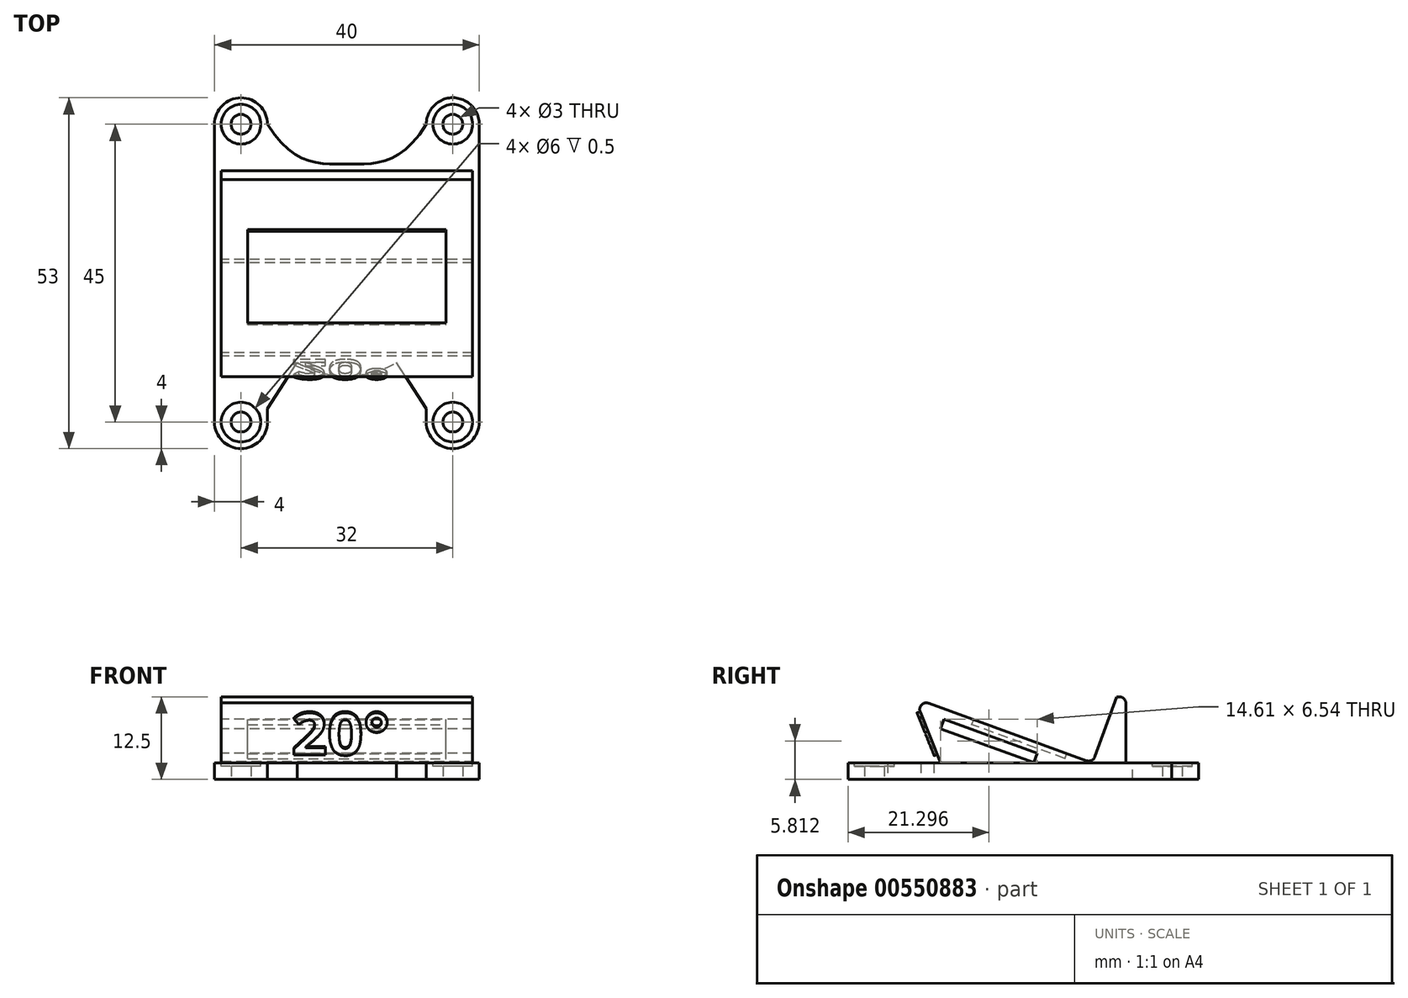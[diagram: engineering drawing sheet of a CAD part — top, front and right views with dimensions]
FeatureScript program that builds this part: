
annotation { "Feature Type Name" : "Feature", "Feature Type Description" : "" }
export const myFeature = defineFeature(function(context is Context, id is Id, definition is map)
    precondition{}
    {
        {
            var Q0;
            Q0=qCreatedBy(makeId("Top.planeOp"),FACE);
            var sketch = newSketch(context, id + "F0", { "sketchPlane" : qUnion([Q0])});
            skCircle(sketch, "E0", {"center": v(-16, 22.5) * mm, "radius": 4 * mm});
            skCircle(sketch, "E1", {"center": v(16, 22.5) * mm, "radius": 4 * mm});
            skCircle(sketch, "E2", {"center": v(-16, -22.5) * mm, "radius": 4 * mm});
            skCircle(sketch, "E3", {"center": v(16, -22.5) * mm, "radius": 4 * mm});
            skLineSegment(sketch, "E4", {"start": v(-20, 22.5) * mm, "end": v(-20, -22.5) * mm});
            skLineSegment(sketch, "E5", {"start": v(20, 22.55) * mm, "end": v(20, -22.5) * mm});
            skLineSegment(sketch, "E6", {"start": v(-12, -22.5) * mm, "end": v(-12, -20.5) * mm});
            skLineSegment(sketch, "E7", {"start": v(12, -22.5) * mm, "end": v(12, -20.5) * mm});
            skLineSegment(sketch, "E8", {"start": v(-12, -20.5) * mm, "end": v(-7.5, -13.5) * mm});
            skLineSegment(sketch, "E9", {"start": v(12, -20.5) * mm, "end": v(7.5, -13.5) * mm});
            skFitSpline(sketch, "E10", {"points": [v(-7.5, -13.5) * mm, v(0, -15.5) * mm, v(7.5, -13.5) * mm], "startDerivative": vector(15, -9) * mm, "endDerivative": vector(15, 9) * mm});
            skFitSpline(sketch, "E11", {"points": [v(-12, 22.5) * mm, v(0, 16.5) * mm, v(12, 22.5) * mm], "startDerivative": vector(24, -39) * mm, "endDerivative": vector(24, 39) * mm});
            skSolve(sketch);
        }
        {
            var Q0;
            Q0 = qSketchRegion(id + "F0", true);
            extrude(context, id + "F1", {"entities" : qUnion([Q0]), "depth" : 2.5 * mm, "offsetDistance" : 25 * mm});
        }
        {
            var Q0;
            Q0=qCreatedBy(makeId("Right.planeOp"),FACE);
            var sketch = newSketch(context, id + "F2", { "sketchPlane" : qUnion([Q0])});
            skLineSegment(sketch, "E12", {"start": v(15.5, 10.16) * mm, "end": v(15.5, 2.5) * mm});
            skLineSegment(sketch, "E13", {"start": v(15.5, 2.5) * mm, "end": v(-12.5, 2.5) * mm});
            skLineSegment(sketch, "E14", {"start": v(-12.5, 2.5) * mm, "end": v(-16.5, 12.5) * mm});
            skLineSegment(sketch, "E15", {"start": v(-16.5, 12.5) * mm, "end": v(15.5, 12.5) * mm});
            skLineSegment(sketch, "E16", {"start": v(15.5, 12.5) * mm, "end": v(15.5, 10.16) * mm});
            skSolve(sketch);
        }
        {
            var Q0;
            Q0 = qSketchRegion(id + "F2", true);
            extrude(context, id + "F3", {"entities" : qUnion([Q0]), "endBound" : BoundingType.SYMMETRIC, "depth" : 38 * mm, "offsetDistance" : 25 * mm});
        }
        {
            var Q0;
            Q0=makeQuery(id+"F3.opExtrude","CAP_FACE",FACE,{"disambiguationData":[OSD([sQuery(id+"F2.wireOp",EDGE,"E12"),sQuery(id+"F2.wireOp",EDGE,"E13"),sQuery(id+"F2.wireOp",EDGE,"E14"),sQuery(id+"F2.wireOp",EDGE,"E15"),sQuery(id+"F2.wireOp",EDGE,"E16")])],"isStart":true});
            var sketch = newSketch(context, id + "F4", { "sketchPlane" : qUnion([Q0])});
            skLineSegment(sketch, "E17", {"start": v(-14.11, 12.5) * mm, "end": v(-10.47, 2.5) * mm});
            skLineSegment(sketch, "E18", {"start": v(-10.47, 2.5) * mm, "end": v(17, 12.5) * mm});
            skLineSegment(sketch, "E19", {"start": v(17, 12.5) * mm, "end": v(-14.11, 12.5) * mm});
            skSolve(sketch);
        }
        {
            var Q0;
            Q0 = qSketchRegion(id + "F4", true);
            extrude(context, id + "F5", {"entities" : qUnion([Q0]), "oppositeDirection" : true, "depth" : 40 * mm, "offsetDistance" : 25 * mm});
        }
        {
            var Q0;
            Q0=makeQuery(id+"F5.opExtrude","SWEPT_BODY",BODY,{"disambiguationData":[OSD([sQuery(id+"F4.wireOp",EDGE,"E17"),sQuery(id+"F4.wireOp",EDGE,"E18"),sQuery(id+"F4.wireOp",EDGE,"E19")])]});
            var Q1;
            Q1=makeQuery(id+"F3.opExtrude","SWEPT_BODY",BODY,{"disambiguationData":[OSD([sQuery(id+"F2.wireOp",EDGE,"E12"),sQuery(id+"F2.wireOp",EDGE,"E13"),sQuery(id+"F2.wireOp",EDGE,"E14"),sQuery(id+"F2.wireOp",EDGE,"E15"),sQuery(id+"F2.wireOp",EDGE,"E16")])]});
            booleanBodies(context, id + "F6", {"operationType" : BooleanOperationType.SUBTRACTION, "tools" : qUnion([Q0]), "targets" : qUnion([Q1])});
        }
        {
            var Q0;
            Q0=sQuery(id+"F0.wireOp",VERTEX,"E0.center");
            var Q1;
            Q1=sQuery(id+"F0.wireOp",VERTEX,"E1.center");
            var Q2;
            Q2=sQuery(id+"F0.wireOp",VERTEX,"E2.center");
            var Q3;
            Q3=sQuery(id+"F0.wireOp",VERTEX,"E3.center");
            var Q4;
            Q4=makeQuery(id+"F1.opExtrude","SWEPT_BODY",BODY,{"disambiguationData":[OSD([sQuery(id+"F0.wireOp",EDGE,"E0"),sQuery(id+"F0.wireOp",EDGE,"E1"),sQuery(id+"F0.wireOp",EDGE,"E2"),sQuery(id+"F0.wireOp",EDGE,"E3"),sQuery(id+"F0.wireOp",EDGE,"E4"),sQuery(id+"F0.wireOp",EDGE,"E5"),sQuery(id+"F0.wireOp",EDGE,"E6"),sQuery(id+"F0.wireOp",EDGE,"E7"),sQuery(id+"F0.wireOp",EDGE,"E8"),sQuery(id+"F0.wireOp",EDGE,"E9"),sQuery(id+"F0.wireOp",EDGE,"E10"),sQuery(id+"F0.wireOp",EDGE,"E11")])]});
            hole(context, id + "F7", {"style" : HoleStyle.SIMPLE, "endStyle" : HoleEndStyle.THROUGH, "oppositeDirection" : true, "holeDiameter" : 3 * mm, "tappedDepth" : 12 * mm, "tapClearance" : 3, "locations" : qUnion([Q0, Q1, Q2, Q3]), "scope" : qUnion([Q4])});
        }
        {
            var Q0;
            Q0=makeQuery(id+"F1.opExtrude","CAP_FACE",FACE,{"disambiguationData":[OSD([sQuery(id+"F0.wireOp",EDGE,"E0"),sQuery(id+"F0.wireOp",EDGE,"E1"),sQuery(id+"F0.wireOp",EDGE,"E2"),sQuery(id+"F0.wireOp",EDGE,"E3"),sQuery(id+"F0.wireOp",EDGE,"E4"),sQuery(id+"F0.wireOp",EDGE,"E5"),sQuery(id+"F0.wireOp",EDGE,"E6"),sQuery(id+"F0.wireOp",EDGE,"E7"),sQuery(id+"F0.wireOp",EDGE,"E8"),sQuery(id+"F0.wireOp",EDGE,"E9"),sQuery(id+"F0.wireOp",EDGE,"E10"),sQuery(id+"F0.wireOp",EDGE,"E11")])],"isStart":false});
            var sketch = newSketch(context, id + "F8", { "sketchPlane" : qUnion([Q0])});
            skCircle(sketch, "E20", {"center": v(-16, 22.5) * mm, "radius": 3 * mm});
            skCircle(sketch, "E21", {"center": v(16, 22.5) * mm, "radius": 3 * mm});
            skCircle(sketch, "E22", {"center": v(-16, -22.5) * mm, "radius": 3 * mm});
            skCircle(sketch, "E23", {"center": v(16, -22.5) * mm, "radius": 3 * mm});
            skSolve(sketch);
        }
        {
            var Q0;
            Q0 = qSketchRegion(id + "F8", true);
            extrude(context, id + "F9", {"entities" : qUnion([Q0]), "oppositeDirection" : true, "depth" : 0.5 * mm, "offsetDistance" : 25 * mm});
        }
        {
            var Q0;
            Q0=makeQuery(id+"F9.opExtrude","SWEPT_BODY",BODY,{"disambiguationData":[OSD([sQuery(id+"F8.wireOp",EDGE,"E20")])]});
            var Q1;
            Q1=makeQuery(id+"F9.opExtrude","SWEPT_BODY",BODY,{"disambiguationData":[OSD([sQuery(id+"F8.wireOp",EDGE,"E21")])]});
            var Q2;
            Q2=makeQuery(id+"F9.opExtrude","SWEPT_BODY",BODY,{"disambiguationData":[OSD([sQuery(id+"F8.wireOp",EDGE,"E22")])]});
            var Q3;
            Q3=makeQuery(id+"F9.opExtrude","SWEPT_BODY",BODY,{"disambiguationData":[OSD([sQuery(id+"F8.wireOp",EDGE,"E23")])]});
            var Q4;
            Q4=makeQuery(id+"F1.opExtrude","SWEPT_BODY",BODY,{"disambiguationData":[OSD([sQuery(id+"F0.wireOp",EDGE,"E0"),sQuery(id+"F0.wireOp",EDGE,"E1"),sQuery(id+"F0.wireOp",EDGE,"E2"),sQuery(id+"F0.wireOp",EDGE,"E3"),sQuery(id+"F0.wireOp",EDGE,"E4"),sQuery(id+"F0.wireOp",EDGE,"E5"),sQuery(id+"F0.wireOp",EDGE,"E6"),sQuery(id+"F0.wireOp",EDGE,"E7"),sQuery(id+"F0.wireOp",EDGE,"E8"),sQuery(id+"F0.wireOp",EDGE,"E9"),sQuery(id+"F0.wireOp",EDGE,"E10"),sQuery(id+"F0.wireOp",EDGE,"E11")])]});
            booleanBodies(context, id + "F10", {"operationType" : BooleanOperationType.SUBTRACTION, "tools" : qUnion([Q0, Q1, Q2, Q3]), "targets" : qUnion([Q4])});
        }
        {
            var Q0;
            Q0=makeQuery(id+"F6.opBoolean","COPY",FACE,{"derivedFrom":makeQuery(id+"F5.opExtrude","SWEPT_FACE",FACE,{"disambiguationData":[OSD([sQuery(id+"F4.wireOp",EDGE,"E18")])]})});
            var sketch = newSketch(context, id + "F11", { "sketchPlane" : qUnion([Q0])});
            skLineSegment(sketch, "E24.bottom", {"start": v(-15, 4.84) * mm, "end": v(15, 4.84) * mm});
            skLineSegment(sketch, "E24.top", {"start": v(-15, -10.16) * mm, "end": v(15, -10.16) * mm});
            skLineSegment(sketch, "E24.left", {"start": v(-15, 4.84) * mm, "end": v(-15, -10.16) * mm});
            skLineSegment(sketch, "E24.right", {"start": v(15, 4.84) * mm, "end": v(15, -10.16) * mm});
            skSolve(sketch);
        }
        {
            var Q0;
            Q0 = qSketchRegion(id + "F11", true);
            extrude(context, id + "F12", {"entities" : qUnion([Q0]), "oppositeDirection" : true, "depth" : 0.8 * mm, "offsetDistance" : 25 * mm});
        }
        {
            var Q0;
            Q0=makeQuery(id+"F12.opExtrude","SWEPT_BODY",BODY,{"disambiguationData":[OSD([sQuery(id+"F11.wireOp",EDGE,"E24.bottom"),sQuery(id+"F11.wireOp",EDGE,"E24.top"),sQuery(id+"F11.wireOp",EDGE,"E24.left"),sQuery(id+"F11.wireOp",EDGE,"E24.right")])]});
            var Q1;
            Q1=makeQuery(id+"F6.opBoolean","SPLIT",BODY,{"disambiguationData":[OD(1.0)],"derivedFrom":makeQuery(id+"F3.opExtrude","SWEPT_BODY",BODY,{"disambiguationData":[OSD([sQuery(id+"F2.wireOp",EDGE,"E12"),sQuery(id+"F2.wireOp",EDGE,"E13"),sQuery(id+"F2.wireOp",EDGE,"E14"),sQuery(id+"F2.wireOp",EDGE,"E15"),sQuery(id+"F2.wireOp",EDGE,"E16")])]})});
            booleanBodies(context, id + "F13", {"operationType" : BooleanOperationType.SUBTRACTION, "tools" : qUnion([Q0]), "targets" : qUnion([Q1])});
        }
        {
            var Q0;
            {var subQ0=sQuery(id+"F2.wireOp",EDGE,"E13");var subQ1=sQuery(id+"F2.wireOp",EDGE,"E14");Q0=makeQuery(id+"F6.opBoolean","SPLIT",FACE,{"disambiguationData":[TD([makeQuery(id+"F3.opExtrude","SWEPT_FACE",FACE,{"disambiguationData":[OSD([subQ1])]})])],"derivedFrom":makeQuery(id+"F3.opExtrude","CAP_FACE",FACE,{"disambiguationData":[OSD([sQuery(id+"F2.wireOp",EDGE,"E12"),subQ0,subQ1,sQuery(id+"F2.wireOp",EDGE,"E15"),sQuery(id+"F2.wireOp",EDGE,"E16")])],"isStart":true})});}
            var sketch = newSketch(context, id + "F14", { "sketchPlane" : qUnion([Q0])});
            skLineSegment(sketch, "E25", {"start": v(-2.1, 3.95) * mm, "end": v(12, 9.08) * mm});
            skLineSegment(sketch, "E26", {"start": v(12, 9.08) * mm, "end": v(12.5, 7.67) * mm});
            skLineSegment(sketch, "E27", {"start": v(12.5, 7.67) * mm, "end": v(-1.59, 2.54) * mm});
            skLineSegment(sketch, "E28", {"start": v(-1.59, 2.54) * mm, "end": v(-2.1, 3.95) * mm});
            skSolve(sketch);
        }
        {
            var Q0;
            Q0 = qSketchRegion(id + "F14", true);
            extrude(context, id + "F15", {"entities" : qUnion([Q0]), "oppositeDirection" : true, "depth" : 40 * mm, "offsetDistance" : 25 * mm});
        }
        {
            var Q0;
            Q0=makeQuery(id+"F15.opExtrude","SWEPT_BODY",BODY,{"disambiguationData":[OSD([sQuery(id+"F14.wireOp",EDGE,"E25"),sQuery(id+"F14.wireOp",EDGE,"E26"),sQuery(id+"F14.wireOp",EDGE,"E27"),sQuery(id+"F14.wireOp",EDGE,"E28")])]});
            var Q1;
            Q1=makeQuery(id+"F6.opBoolean","SPLIT",BODY,{"disambiguationData":[OD(1.0)],"derivedFrom":makeQuery(id+"F3.opExtrude","SWEPT_BODY",BODY,{"disambiguationData":[OSD([sQuery(id+"F2.wireOp",EDGE,"E12"),sQuery(id+"F2.wireOp",EDGE,"E13"),sQuery(id+"F2.wireOp",EDGE,"E14"),sQuery(id+"F2.wireOp",EDGE,"E15"),sQuery(id+"F2.wireOp",EDGE,"E16")])]})});
            booleanBodies(context, id + "F16", {"operationType" : BooleanOperationType.SUBTRACTION, "tools" : qUnion([Q0]), "targets" : qUnion([Q1])});
        }
        {
            var Q0;
            Q0=makeQuery(id+"F1.opExtrude","SWEPT_BODY",BODY,{"disambiguationData":[OSD([sQuery(id+"F0.wireOp",EDGE,"E0"),sQuery(id+"F0.wireOp",EDGE,"E1"),sQuery(id+"F0.wireOp",EDGE,"E2"),sQuery(id+"F0.wireOp",EDGE,"E3"),sQuery(id+"F0.wireOp",EDGE,"E4"),sQuery(id+"F0.wireOp",EDGE,"E5"),sQuery(id+"F0.wireOp",EDGE,"E6"),sQuery(id+"F0.wireOp",EDGE,"E7"),sQuery(id+"F0.wireOp",EDGE,"E8"),sQuery(id+"F0.wireOp",EDGE,"E9"),sQuery(id+"F0.wireOp",EDGE,"E10"),sQuery(id+"F0.wireOp",EDGE,"E11")])]});
            var Q1;
            Q1=makeQuery(id+"F6.opBoolean","SPLIT",BODY,{"disambiguationData":[OD(0.0)],"derivedFrom":makeQuery(id+"F3.opExtrude","SWEPT_BODY",BODY,{"disambiguationData":[OSD([sQuery(id+"F2.wireOp",EDGE,"E12"),sQuery(id+"F2.wireOp",EDGE,"E13"),sQuery(id+"F2.wireOp",EDGE,"E14"),sQuery(id+"F2.wireOp",EDGE,"E15"),sQuery(id+"F2.wireOp",EDGE,"E16")])]})});
            var Q2;
            Q2=makeQuery(id+"F6.opBoolean","SPLIT",BODY,{"disambiguationData":[OD(1.0)],"derivedFrom":makeQuery(id+"F3.opExtrude","SWEPT_BODY",BODY,{"disambiguationData":[OSD([sQuery(id+"F2.wireOp",EDGE,"E12"),sQuery(id+"F2.wireOp",EDGE,"E13"),sQuery(id+"F2.wireOp",EDGE,"E14"),sQuery(id+"F2.wireOp",EDGE,"E15"),sQuery(id+"F2.wireOp",EDGE,"E16")])]})});
            booleanBodies(context, id + "F17", {"operationType" : BooleanOperationType.UNION, "tools" : qUnion([Q0, Q1, Q2])});
        }
        {
            var Q0;
            Q0=makeQuery(id+"F3.opExtrude","SWEPT_EDGE",EDGE,{"disambiguationData":[OSD([sQuery(id+"F2.wireOp",EDGE,"E13"),sQuery(id+"F2.wireOp",EDGE,"E14")])]});
            var Q1;
            Q1=makeQuery(id+"F6.opBoolean","INTERSECT",EDGE,{"derivedFrom":[makeQuery(id+"F3.opExtrude","SWEPT_FACE",FACE,{"disambiguationData":[OSD([sQuery(id+"F2.wireOp",EDGE,"E14")])]}),makeQuery(id+"F5.opExtrude","SWEPT_FACE",FACE,{"disambiguationData":[OSD([sQuery(id+"F4.wireOp",EDGE,"E18")])]})]});
            var Q2;
            Q2=makeQuery(id+"F3.opExtrude","SWEPT_EDGE",EDGE,{"disambiguationData":[OSD([sQuery(id+"F2.wireOp",EDGE,"E15"),sQuery(id+"F2.wireOp",EDGE,"E16")])]});
            var Q3;
            {var subQ0=sQuery(id+"F2.wireOp",EDGE,"E13");var subQ2=sQuery(id+"F4.wireOp",EDGE,"E18");var subQ3=sQuery(id+"F4.wireOp",EDGE,"E17");var subQ4=makeQuery(id+"F5.opExtrude","SWEPT_EDGE",EDGE,{"disambiguationData":[OSD([subQ0,subQ3,subQ2])]});Q3=makeQuery(id+"F17.opBoolean","MERGE",EDGE,{"derivedFrom":[makeQuery(id+"F6.opBoolean","COPY",EDGE,{"disambiguationData":[topologyDisambiguationEdgeConnected([makeQuery(id+"F5.opExtrude","SWEPT_FACE",FACE,{"disambiguationData":[OSD([subQ3])]})])],"derivedFrom":subQ4}),makeQuery(id+"F6.opBoolean","COPY",EDGE,{"disambiguationData":[topologyDisambiguationEdgeConnected([makeQuery(id+"F5.opExtrude","SWEPT_FACE",FACE,{"disambiguationData":[OSD([subQ2])]})])],"derivedFrom":subQ4})]});}
            fillet(context, id + "F18", {"entities" : qUnion([Q0, Q1, Q2, Q3]), "radius" : 1 * mm, "tangentPropagation" : true, "allowEdgeOverflow" : false});
        }
        {
            var Q0;
            Q0=makeQuery(id+"F3.opExtrude","SWEPT_FACE",FACE,{"disambiguationData":[OSD([sQuery(id+"F2.wireOp",EDGE,"E14")])]});
            var sketch = newSketch(context, id + "F19", { "sketchPlane" : qUnion([Q0])});
            skText(sketch, "E29", { "text": "20°", "fontName": "OpenSans-Bold.ttf"});
            const initialGuessF19  = {"E29": [-0.00837, 0.00844, 1, 0, 0.00683]};
            skSetInitialGuess(sketch, initialGuessF19);
            skSolve(sketch);
        }
        {
            var Q0;
            Q0 = qSketchRegion(id + "F19", true);
            extrude(context, id + "F20", {"entities" : qUnion([Q0]), "operationType" : NewBodyOperationType.ADD, "depth" : 0.5 * mm, "offsetDistance" : 25 * mm});
        }
    });
